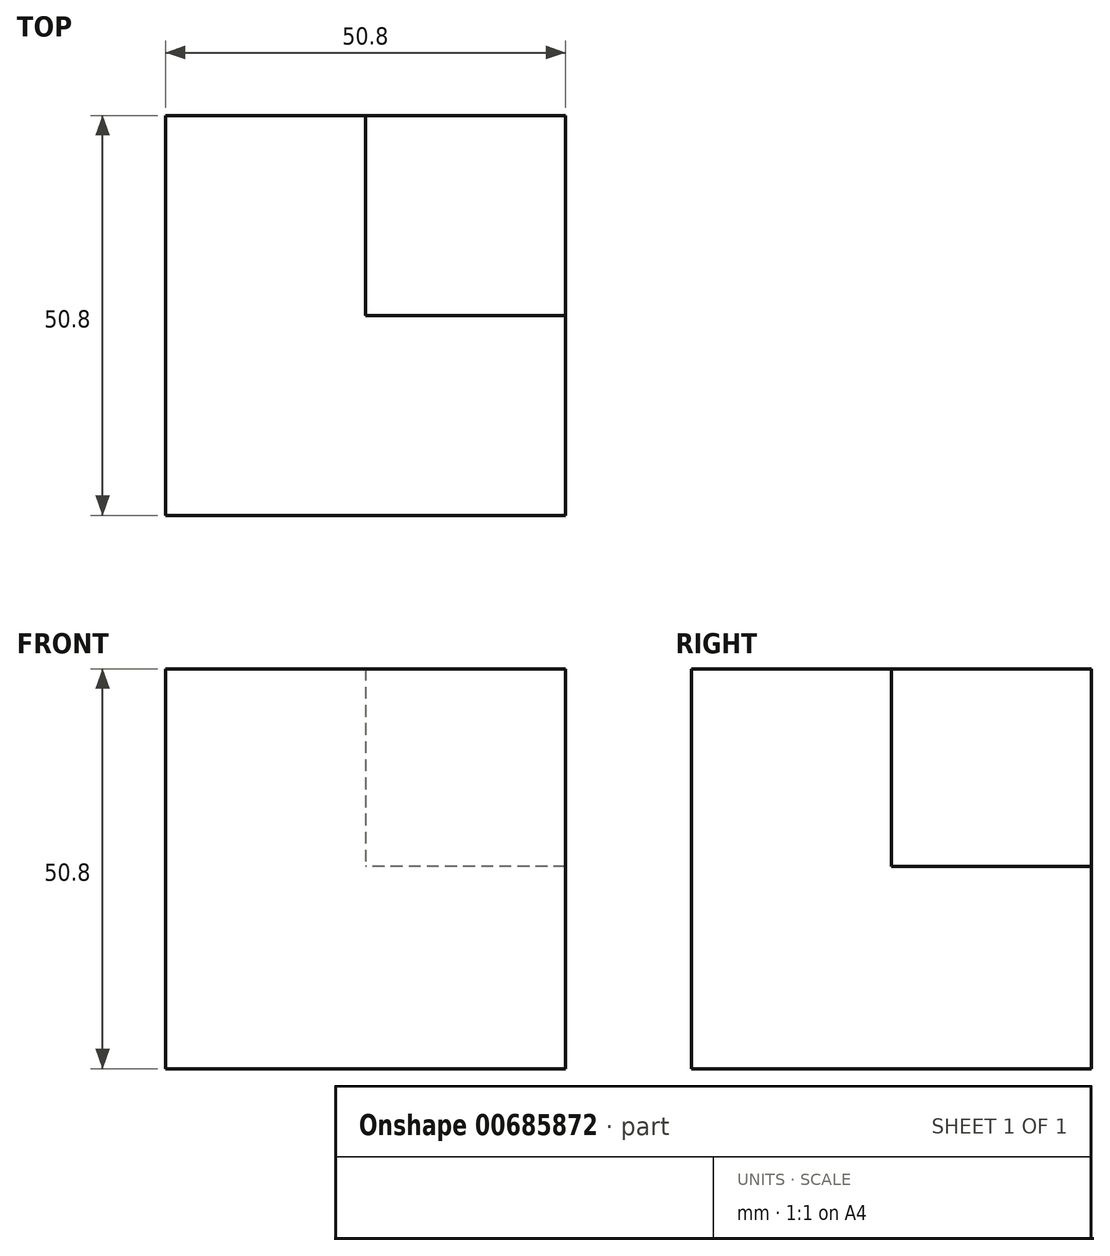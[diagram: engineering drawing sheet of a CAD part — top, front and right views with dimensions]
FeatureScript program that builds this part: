
annotation { "Feature Type Name" : "Feature", "Feature Type Description" : "" }
export const myFeature = defineFeature(function(context is Context, id is Id, definition is map)
    precondition{}
    {
        {
            var Q0;
            Q0=qCreatedBy(makeId("Front.planeOp"),FACE);
            var sketch = newSketch(context, id + "F0", { "sketchPlane" : qUnion([Q0])});
            skLineSegment(sketch, "E0.bottom", {"start": v(0, 0) * mm, "end": v(-50.8, 0) * mm});
            skLineSegment(sketch, "E0.top", {"start": v(0, 50.8) * mm, "end": v(-50.8, 50.8) * mm});
            skLineSegment(sketch, "E0.left", {"start": v(0, 0) * mm, "end": v(0, 50.8) * mm});
            skLineSegment(sketch, "E0.right", {"start": v(-50.8, 0) * mm, "end": v(-50.8, 50.8) * mm});
            skSolve(sketch);
        }
        {
            var Q0;
            Q0 = qSketchRegion(id + "F0", true);
            extrude(context, id + "F1", {"entities" : qUnion([Q0]), "depth" : 50.8 * mm, "offsetDistance" : 25.4 * mm});
        }
        {
            var Q0;
            Q0=qCreatedBy(makeId("Front.planeOp"),FACE);
            var sketch = newSketch(context, id + "F2", { "sketchPlane" : qUnion([Q0])});
            skLineSegment(sketch, "E1.bottom", {"start": v(0, 51.1) * mm, "end": v(-25.4, 51.1) * mm});
            skLineSegment(sketch, "E1.top", {"start": v(0, 25.7) * mm, "end": v(-25.4, 25.7) * mm});
            skLineSegment(sketch, "E1.left", {"start": v(0, 51.1) * mm, "end": v(0, 25.7) * mm});
            skLineSegment(sketch, "E1.right", {"start": v(-25.4, 51.1) * mm, "end": v(-25.4, 25.7) * mm});
            skSolve(sketch);
        }
        {
            var Q0;
            Q0=makeQuery(id+"F2.imprint","IMPRINT",FACE,{"disambiguationData":[TD([[makeQuery(id+"F2.imprint","IMPRINT",EDGE,{"derivedFrom":sQuery(id+"F2.wireOp",EDGE,"E1.bottom")}),1.0]])]});
            extrude(context, id + "F3", {"entities" : qUnion([Q0]), "operationType" : NewBodyOperationType.REMOVE, "depth" : 25.4 * mm, "offsetDistance" : 25.4 * mm});
        }
    });
